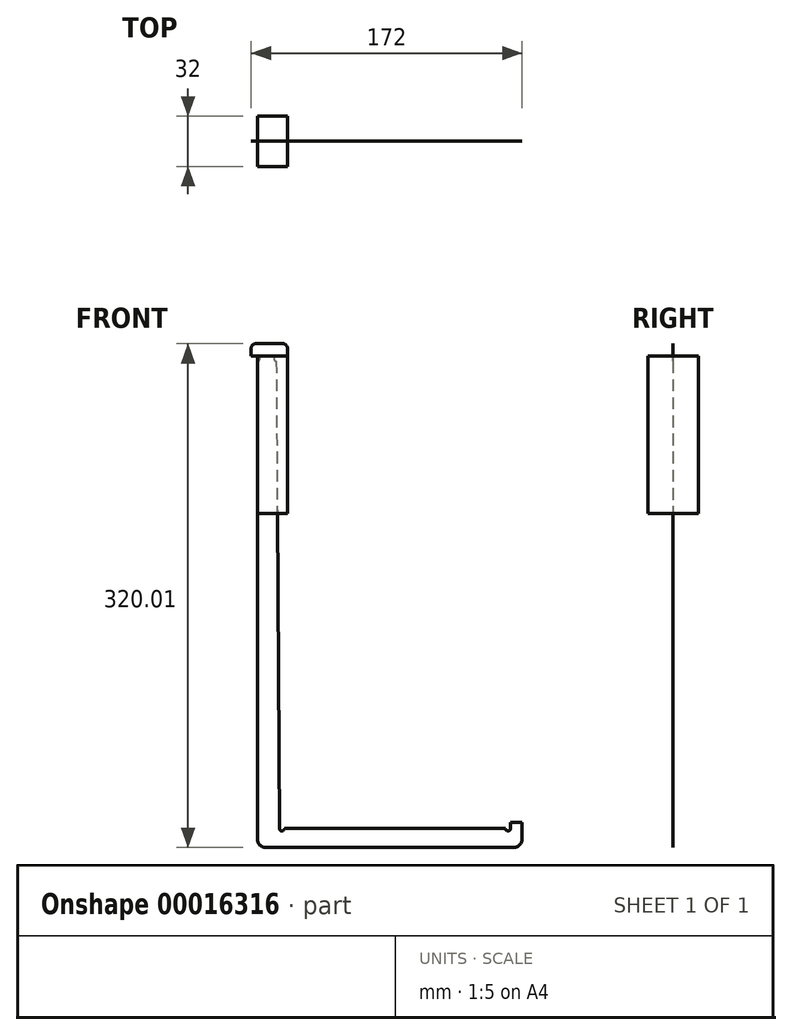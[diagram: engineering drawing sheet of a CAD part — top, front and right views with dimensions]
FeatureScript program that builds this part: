
annotation { "Feature Type Name" : "Feature", "Feature Type Description" : "" }
export const myFeature = defineFeature(function(context is Context, id is Id, definition is map)
    precondition{}
    {
        {
            var Q0;
            Q0=qCreatedBy(makeId("Front.planeOp"),FACE);
            var sketch = newSketch(context, id + "F0", { "sketchPlane" : qUnion([Q0])});
            skLineSegment(sketch, "E0.bottom", {"start": v(-39.7, 73.1) * mm, "end": v(-27.7, 73.1) * mm});
            skLineSegment(sketch, "E0.top", {"start": v(-34.7, -246.9) * mm, "end": v(-27.75, -246.9) * mm});
            skLineSegment(sketch, "E0.left", {"start": v(-39.7, 61.93) * mm, "end": v(-39.7, -241.9) * mm});
            skLineSegment(sketch, "E1.bottom", {"start": v(-27.75, -246.9) * mm, "end": v(123.3, -246.9) * mm});
            skLineSegment(sketch, "E1.right", {"start": v(128.3, -241.9) * mm, "end": v(128.3, -234.9) * mm});
            skLineSegment(sketch, "E2.top", {"start": v(128.3, -230.9) * mm, "end": v(121.04, -230.9) * mm});
            skLineSegment(sketch, "E2.left", {"start": v(128.3, -234.9) * mm, "end": v(128.3, -230.9) * mm});
            skLineSegment(sketch, "E2.right", {"start": v(121.04, -234.87) * mm, "end": v(121.04, -230.9) * mm});
            skLineSegment(sketch, "E3.top", {"start": v(-27.7, 65.1) * mm, "end": v(-20.65, 65.1) * mm});
            skLineSegment(sketch, "E3.right", {"start": v(-20.64, 68.1) * mm, "end": v(-20.65, 65.1) * mm});
            skLineSegment(sketch, "E4.bottom", {"start": v(-39.7, 73.1) * mm, "end": v(-40.7, 73.1) * mm});
            skLineSegment(sketch, "E4.top", {"start": v(-39.7, 65.1) * mm, "end": v(-43.7, 65.1) * mm});
            skLineSegment(sketch, "E4.right", {"start": v(-43.7, 70.1) * mm, "end": v(-43.7, 65.1) * mm});
            skLineSegment(sketch, "E5", {"start": v(-43.7, 65.1) * mm, "end": v(-43.7, -234.9) * mm, "construction": true});
            skLineSegment(sketch, "E6", {"start": v(-43.7, -234.9) * mm, "end": v(-25.7, -234.9) * mm, "construction": true});
            skLineSegment(sketch, "E7", {"start": v(121.04, -230.9) * mm, "end": v(-28.96, -230.9) * mm, "construction": true});
            skPoint(sketch, "E8.visualSharp", {"position": v(-39.7, -246.9) * mm});
            skArc(sketch, "E8.filletArc", {"start": v(-39.7, -241.9) * mm, "mid": v(-38.23, -245.44) * mm, "end": v(-34.7, -246.9) * mm});
            skPoint(sketch, "E9.visualSharp", {"position": v(128.3, -246.9) * mm});
            skArc(sketch, "E9.filletArc", {"start": v(123.3, -246.9) * mm, "mid": v(126.84, -245.44) * mm, "end": v(128.3, -241.9) * mm});
            skPoint(sketch, "E10.visualSharp", {"position": v(-43.7, 73.1) * mm});
            skArc(sketch, "E10.filletArc", {"start": v(-40.7, 73.1) * mm, "mid": v(-42.82, 72.23) * mm, "end": v(-43.7, 70.1) * mm});
            skPoint(sketch, "E11.visualSharp", {"position": v(-20.64, 73.1) * mm});
            skArc(sketch, "E12", {"start": v(-39.7, 61.93) * mm, "mid": v(-38.1, 63.52) * mm, "end": v(-39.7, 65.1) * mm});
            skArc(sketch, "E13", {"start": v(-27.7, 65.1) * mm, "mid": v(-29.3, 63.55) * mm, "end": v(-27.77, 61.93) * mm});
            skLineSegment(sketch, "E14.trimOffspring", {"start": v(-27.77, 61.93) * mm, "end": v(-25.7, -234.9) * mm});
            skArc(sketch, "E15", {"start": v(-25.7, -234.89) * mm, "mid": v(-24.11, -236.47) * mm, "end": v(-22.53, -234.87) * mm});
            skLineSegment(sketch, "E16.trimOffspring", {"start": v(-22.53, -234.87) * mm, "end": v(117.87, -234.87) * mm});
            skArc(sketch, "E17", {"start": v(117.87, -234.87) * mm, "mid": v(119.45, -236.45) * mm, "end": v(121.04, -234.87) * mm});
            skLineSegment(sketch, "E18", {"start": v(-20.64, 68.1) * mm, "end": v(-20.64, 70.1) * mm});
            skArc(sketch, "E19.filletArc", {"start": v(-20.64, 70.1) * mm, "mid": v(-21.52, 72.23) * mm, "end": v(-23.64, 73.1) * mm});
            skLineSegment(sketch, "E20", {"start": v(-39.7, 51.8) * mm, "end": v(-27.7, 51.8) * mm, "construction": true});
            skLineSegment(sketch, "E21", {"start": v(-23.64, 73.1) * mm, "end": v(-27.7, 73.1) * mm});
            skSolve(sketch);
        }
        {
            var Q0;
            Q0=qCreatedBy(makeId("Front.planeOp"),FACE);
            var sketch = newSketch(context, id + "F1", { "sketchPlane" : qUnion([Q0])});
            skLineSegment(sketch, "E22.bottom", {"start": v(-20.64, 65.1) * mm, "end": v(-39.69, 65.1) * mm});
            skLineSegment(sketch, "E22.top", {"start": v(-20.64, -34.9) * mm, "end": v(-39.69, -34.9) * mm});
            skLineSegment(sketch, "E22.left", {"start": v(-20.64, 65.1) * mm, "end": v(-20.64, -34.9) * mm});
            skLineSegment(sketch, "E22.right", {"start": v(-39.69, 65.1) * mm, "end": v(-39.69, -34.9) * mm});
            skSolve(sketch);
        }
        {
            var Q0;
            Q0=makeQuery(id+"F0.imprint","IMPRINT",FACE,{"disambiguationData":[TD([[makeQuery(id+"F0.imprint","IMPRINT",EDGE,{"derivedFrom":sQuery(id+"F0.wireOp",EDGE,"E0.bottom")}),-1.0]])]});
            extrude(context, id + "F2", {"entities" : qUnion([Q0]), "endBound" : BoundingType.SYMMETRIC, "depth" : 1 / 203.2 * mm});
        }
        {
            var Q0;
            Q0=makeQuery(id+"F1.imprint","IMPRINT",FACE,{"disambiguationData":[TD([[makeQuery(id+"F1.imprint","IMPRINT",EDGE,{"derivedFrom":sQuery(id+"F1.wireOp",EDGE,"E22.bottom")}),1.0]])]});
            extrude(context, id + "F3", {"entities" : qUnion([Q0]), "endBound" : BoundingType.SYMMETRIC, "depth" : 32 * mm});
        }
    });
